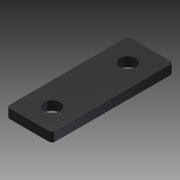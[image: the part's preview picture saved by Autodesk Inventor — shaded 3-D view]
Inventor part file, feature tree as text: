
AUTODESK INVENTOR PART (.ipt)
format: ipt  version: 2015 (Build 190159000, 159)  size: 85,504 bytes
history: native  units: mm
features: extrude x1, fillet x1
ambient origin geometry x8: Origin, YZ Plane, XZ Plane, XY Plane, X Axis, Y Axis, Z Axis, Center Point
bodies: Solid1 (feature_tree)
feature tree (2):
  extrude  "Extrusión1"  Depth=40.0mm
  fillet  "Empalme1"  Radius=15.0mm
